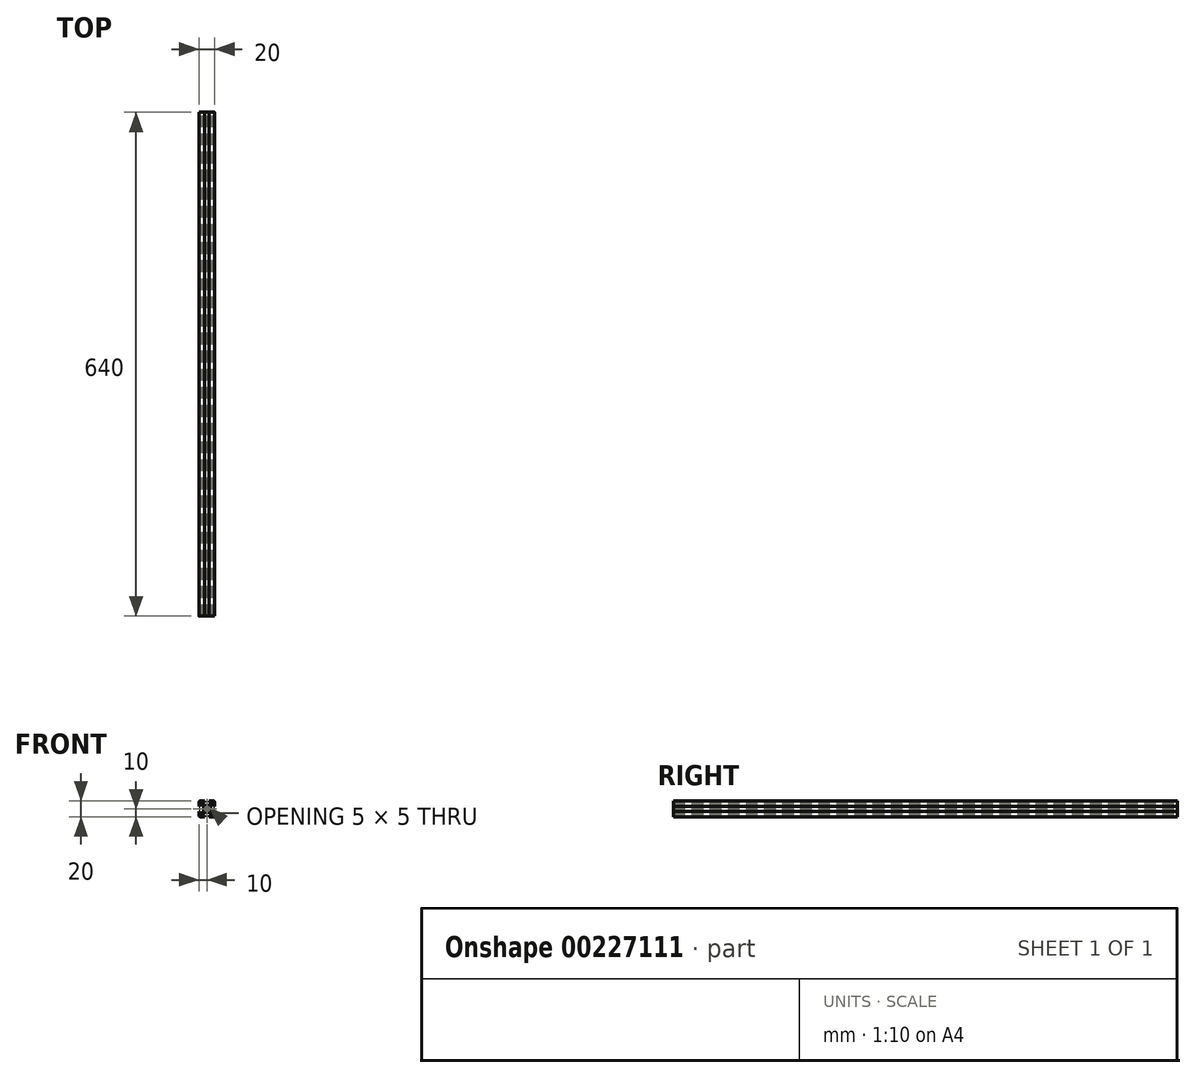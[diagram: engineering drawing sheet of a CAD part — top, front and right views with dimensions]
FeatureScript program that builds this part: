
annotation { "Feature Type Name" : "Feature", "Feature Type Description" : "" }
export const myFeature = defineFeature(function(context is Context, id is Id, definition is map)
    precondition{}
    {
        {
            var Q0;
            Q0=qCreatedBy(makeId("Front.planeOp"),FACE);
            var sketch = newSketch(context, id + "F0", { "sketchPlane" : qUnion([Q0])});
            skLineSegment(sketch, "E0.bottom", {"start": v(8.5, -10) * mm, "end": v(3, -10) * mm});
            skLineSegment(sketch, "E0.top", {"start": v(8.5, 10) * mm, "end": v(3, 10) * mm});
            skLineSegment(sketch, "E0.left", {"start": v(10, -8.5) * mm, "end": v(10, -3) * mm});
            skLineSegment(sketch, "E0.right", {"start": v(-10, -8.5) * mm, "end": v(-10, -3) * mm});
            skPoint(sketch, "E0.middle", {"position": v(0, 0) * mm});
            skLineSegment(sketch, "E1.bottom", {"start": v(6, -8.5) * mm, "end": v(3, -8.5) * mm});
            skLineSegment(sketch, "E1.top", {"start": v(6, 8.5) * mm, "end": v(3, 8.5) * mm});
            skLineSegment(sketch, "E1.left", {"start": v(8.5, -6) * mm, "end": v(8.5, -3) * mm});
            skLineSegment(sketch, "E1.right", {"start": v(-8.5, -6) * mm, "end": v(-8.5, -3) * mm});
            skLineSegment(sketch, "E2.bottom", {"start": v(3.44, -4.5) * mm, "end": v(-3.44, -4.5) * mm});
            skLineSegment(sketch, "E2.top", {"start": v(3.44, 4.5) * mm, "end": v(-3.44, 4.5) * mm});
            skLineSegment(sketch, "E2.left", {"start": v(4.5, -3.44) * mm, "end": v(4.5, 3.44) * mm});
            skLineSegment(sketch, "E2.right", {"start": v(-4.5, -3.44) * mm, "end": v(-4.5, 3.44) * mm});
            skLineSegment(sketch, "E3.bottom", {"start": v(8.5, -6) * mm, "end": v(7.06, -6) * mm});
            skLineSegment(sketch, "E3.top", {"start": v(8.5, 6) * mm, "end": v(7.06, 6) * mm});
            skLineSegment(sketch, "E4.left", {"start": v(6, -8.5) * mm, "end": v(6, -7.06) * mm});
            skLineSegment(sketch, "E4.right", {"start": v(-6, -8.5) * mm, "end": v(-6, -7.06) * mm});
            skPoint(sketch, "E5.orphan", {"position": v(-8.5, 8.5) * mm});
            skPoint(sketch, "E6.orphan", {"position": v(8.5, 8.5) * mm});
            skPoint(sketch, "E7.orphan", {"position": v(8.5, -8.5) * mm});
            skPoint(sketch, "E8.orphan", {"position": v(-8.5, -8.5) * mm});
            skLineSegment(sketch, "E9.trimOffspring", {"start": v(-6, 7.06) * mm, "end": v(-6, 8.5) * mm});
            skLineSegment(sketch, "E10.trimOffspring", {"start": v(-7.06, 6) * mm, "end": v(-8.5, 6) * mm});
            skLineSegment(sketch, "E11.trimOffspring", {"start": v(6, 7.06) * mm, "end": v(6, 8.5) * mm});
            skLineSegment(sketch, "E12.trimOffspring", {"start": v(-7.06, -6) * mm, "end": v(-8.5, -6) * mm});
            skLineSegment(sketch, "E13", {"start": v(-10, 10) * mm, "end": v(0, 0) * mm, "construction": true});
            skLineSegment(sketch, "E14", {"start": v(10, 10) * mm, "end": v(0, 0) * mm, "construction": true});
            skLineSegment(sketch, "E15", {"start": v(-6, 7.06) * mm, "end": v(-3.44, 4.5) * mm});
            skPoint(sketch, "E15.endSnap0", {"position": v(7.25, -6) * mm});
            skLineSegment(sketch, "E16", {"start": v(6, -7.06) * mm, "end": v(3.44, -4.5) * mm});
            skLineSegment(sketch, "E17", {"start": v(7.06, 6) * mm, "end": v(4.5, 3.44) * mm});
            skLineSegment(sketch, "E18", {"start": v(6, 7.06) * mm, "end": v(3.44, 4.5) * mm});
            skPoint(sketch, "E19.orphan", {"position": v(6, -6) * mm});
            skPoint(sketch, "E20.orphan", {"position": v(-4.5, -4.5) * mm});
            skPoint(sketch, "E21.orphan", {"position": v(-4.5, 4.5) * mm});
            skPoint(sketch, "E22.orphan", {"position": v(4.5, 4.5) * mm});
            skPoint(sketch, "E23.orphan", {"position": v(4.5, -4.5) * mm});
            skLineSegment(sketch, "E24.trimOffspring", {"start": v(4.5, -3.44) * mm, "end": v(7.06, -6) * mm});
            skLineSegment(sketch, "E25.trimOffspring", {"start": v(-3.44, -4.5) * mm, "end": v(-6, -7.06) * mm});
            skLineSegment(sketch, "E26.trimOffspring", {"start": v(-4.5, -3.44) * mm, "end": v(-7.06, -6) * mm});
            skLineSegment(sketch, "E27.trimOffspring", {"start": v(-4.5, 3.44) * mm, "end": v(-7.06, 6) * mm});
            skLineSegment(sketch, "E28.bottom", {"start": v(8.5, -3) * mm, "end": v(10, -3) * mm});
            skLineSegment(sketch, "E28.top", {"start": v(8.5, 3) * mm, "end": v(10, 3) * mm});
            skPoint(sketch, "E28.middle", {"position": v(10, 0) * mm});
            skLineSegment(sketch, "E29.left", {"start": v(3, 8.5) * mm, "end": v(3, 10) * mm});
            skLineSegment(sketch, "E29.right", {"start": v(-3, 8.5) * mm, "end": v(-3, 10) * mm});
            skPoint(sketch, "E29.middle", {"position": v(0, 10) * mm});
            skLineSegment(sketch, "E30.bottom", {"start": v(-8.5, 3) * mm, "end": v(-10, 3) * mm});
            skLineSegment(sketch, "E30.top", {"start": v(-8.5, -3) * mm, "end": v(-10, -3) * mm});
            skPoint(sketch, "E30.middle", {"position": v(-10, 0) * mm});
            skLineSegment(sketch, "E31.left", {"start": v(3, -8.5) * mm, "end": v(3, -10) * mm});
            skLineSegment(sketch, "E31.right", {"start": v(-3, -8.5) * mm, "end": v(-3, -10) * mm});
            skPoint(sketch, "E31.middle", {"position": v(0, -10) * mm});
            skPoint(sketch, "E32.orphan", {"position": v(3, 11.5) * mm});
            skPoint(sketch, "E33.orphan", {"position": v(-3, 11.5) * mm});
            skLineSegment(sketch, "E34.trimOffspring", {"start": v(-3, 10) * mm, "end": v(-8.5, 10) * mm});
            skLineSegment(sketch, "E35.trimOffspring", {"start": v(-3, 8.5) * mm, "end": v(-6, 8.5) * mm});
            skPoint(sketch, "E28.right.end.orphan", {"position": v(11.5, 3) * mm});
            skPoint(sketch, "E36.orphan", {"position": v(11.5, -3) * mm});
            skLineSegment(sketch, "E37.trimOffspring", {"start": v(10, 3) * mm, "end": v(10, 8.5) * mm});
            skLineSegment(sketch, "E38.trimOffspring", {"start": v(8.5, 3) * mm, "end": v(8.5, 6) * mm});
            skPoint(sketch, "E39.orphan", {"position": v(3, -11.5) * mm});
            skPoint(sketch, "E40.orphan", {"position": v(-3, -11.5) * mm});
            skLineSegment(sketch, "E41.trimOffspring", {"start": v(-3, -10) * mm, "end": v(-8.5, -10) * mm});
            skLineSegment(sketch, "E42.trimOffspring", {"start": v(-3, -8.5) * mm, "end": v(-6, -8.5) * mm});
            skPoint(sketch, "E30.right.end.orphan", {"position": v(-11.5, -3) * mm});
            skPoint(sketch, "E43.orphan", {"position": v(-11.5, 3) * mm});
            skLineSegment(sketch, "E44.trimOffspring", {"start": v(-10, 3) * mm, "end": v(-10, 8.5) * mm});
            skLineSegment(sketch, "E45.trimOffspring", {"start": v(-8.5, 3) * mm, "end": v(-8.5, 6) * mm});
            skLineSegment(sketch, "E46.trimOffspring", {"start": v(0, 0) * mm, "end": v(10, -10) * mm, "construction": true});
            skLineSegment(sketch, "E47.trimOffspring", {"start": v(0, 0) * mm, "end": v(-10, -10) * mm, "construction": true});
            skArc(sketch, "E48", {"start": v(1.16, 2.22) * mm, "mid": v(0, 2.5) * mm, "end": v(-1.16, 2.22) * mm});
            skLineSegment(sketch, "E49", {"start": v(-2.5, -1.44) * mm, "end": v(1.44, 2.5) * mm});
            skLineSegment(sketch, "E50", {"start": v(2.5, 1.44) * mm, "end": v(-1.44, -2.5) * mm});
            skLineSegment(sketch, "E51", {"start": v(1.44, -2.5) * mm, "end": v(-2.5, 1.44) * mm});
            skLineSegment(sketch, "E52", {"start": v(-1.44, 2.5) * mm, "end": v(2.5, -1.44) * mm});
            skLineSegment(sketch, "E53", {"start": v(2.5, 1.44) * mm, "end": v(2.5, -1.44) * mm, "construction": true});
            skLineSegment(sketch, "E54", {"start": v(1.44, -2.5) * mm, "end": v(-1.44, -2.5) * mm, "construction": true});
            skLineSegment(sketch, "E55", {"start": v(-2.5, -1.44) * mm, "end": v(-2.5, 1.44) * mm, "construction": true});
            skLineSegment(sketch, "E56", {"start": v(-1.44, 2.5) * mm, "end": v(1.44, 2.5) * mm, "construction": true});
            skLineSegment(sketch, "E57", {"start": v(-1.44, 2.5) * mm, "end": v(-2.5, 1.44) * mm});
            skLineSegment(sketch, "E58", {"start": v(1.44, 2.5) * mm, "end": v(2.5, 1.44) * mm});
            skLineSegment(sketch, "E59", {"start": v(2.5, -1.44) * mm, "end": v(1.44, -2.5) * mm});
            skLineSegment(sketch, "E60", {"start": v(-1.44, -2.5) * mm, "end": v(-2.5, -1.44) * mm});
            skArc(sketch, "E61.trimOffspring", {"start": v(-2.22, 1.16) * mm, "mid": v(-2.5, 0) * mm, "end": v(-2.22, -1.16) * mm});
            skArc(sketch, "E62.trimOffspring", {"start": v(-1.16, -2.22) * mm, "mid": v(0, -2.5) * mm, "end": v(1.16, -2.22) * mm});
            skArc(sketch, "E63.trimOffspring", {"start": v(2.22, -1.16) * mm, "mid": v(2.5, 0) * mm, "end": v(2.22, 1.16) * mm});
            skPoint(sketch, "E64.visualSharp", {"position": v(10, 10) * mm});
            skArc(sketch, "E64.filletArc", {"start": v(10, 8.5) * mm, "mid": v(9.56, 9.56) * mm, "end": v(8.5, 10) * mm});
            skPoint(sketch, "E65.visualSharp", {"position": v(10, -10) * mm});
            skArc(sketch, "E65.filletArc", {"start": v(8.5, -10) * mm, "mid": v(9.56, -9.56) * mm, "end": v(10, -8.5) * mm});
            skPoint(sketch, "E66.visualSharp", {"position": v(-10, -10) * mm});
            skArc(sketch, "E66.filletArc", {"start": v(-10, -8.5) * mm, "mid": v(-9.56, -9.56) * mm, "end": v(-8.5, -10) * mm});
            skPoint(sketch, "E67.visualSharp", {"position": v(-10, 10) * mm});
            skArc(sketch, "E67.filletArc", {"start": v(-8.5, 10) * mm, "mid": v(-9.56, 9.56) * mm, "end": v(-10, 8.5) * mm});
            skSolve(sketch);
        }
        {
            assignVariable(context, id + "F2", {"name" : "Length", "anyValue" : 640});
        }
        {
            var Q0;
            Q0=qSketchRegion(id+"F0",true);
            extrude(context, id + "F1", {"entities" : qUnion([Q0]), "depth" : (getVariable(context, 'Length')) * mm});
        }
    });
